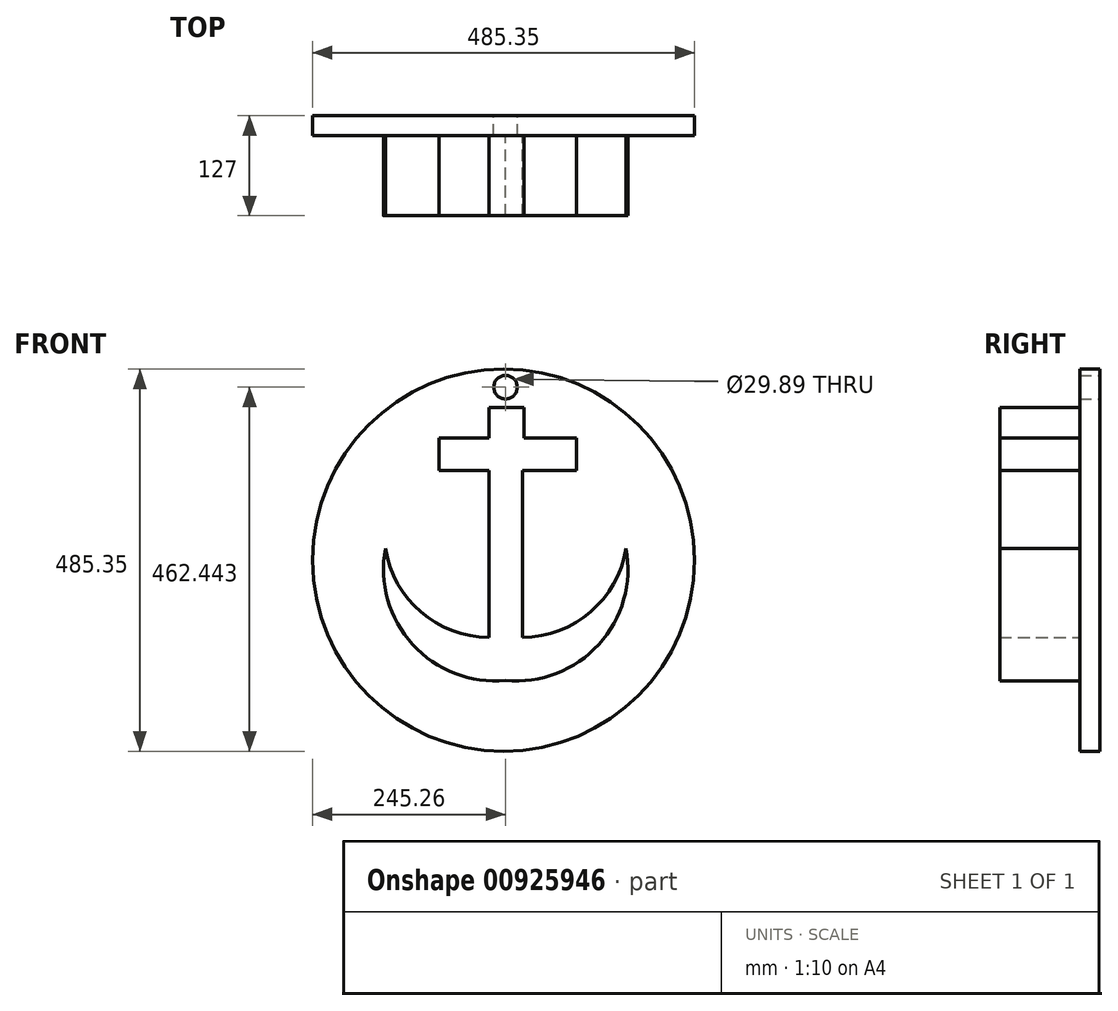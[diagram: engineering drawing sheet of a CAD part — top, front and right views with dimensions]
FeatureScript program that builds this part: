
annotation { "Feature Type Name" : "Feature", "Feature Type Description" : "" }
export const myFeature = defineFeature(function(context is Context, id is Id, definition is map)
    precondition{}
    {
        {
            var Q0;
            Q0=qCreatedBy(makeId("Front.planeOp"),FACE);
            var sketch = newSketch(context, id + "F0", { "sketchPlane" : qUnion([Q0])});
            skLineSegment(sketch, "E0", {"start": v(-148.32, 98.82) * mm, "end": v(-148.32, -113.03) * mm});
            skLineSegment(sketch, "E1.MirrorCS", {"start": v(-105.3, 98.82) * mm, "end": v(-105.3, -113.03) * mm});
            skArc(sketch, "E2", {"start": v(-279.63, 0) * mm, "mid": v(-234.63, -80.51) * mm, "end": v(-148.32, -113.03) * mm});
            skArc(sketch, "E3.MirrorCS", {"start": v(26, 0) * mm, "mid": v(-18.98, -80.51) * mm, "end": v(-105.3, -113.03) * mm});
            skArc(sketch, "E4", {"start": v(-279.63, 0) * mm, "mid": v(-245.04, -121.95) * mm, "end": v(-126.8, -167.65) * mm});
            skArc(sketch, "E5.MirrorCS", {"start": v(26, 0) * mm, "mid": v(-8.57, -121.95) * mm, "end": v(-126.8, -167.65) * mm});
            skLineSegment(sketch, "E6.bottom", {"start": v(-211.77, 140.2) * mm, "end": v(-148.32, 140.2) * mm});
            skLineSegment(sketch, "E6.top", {"start": v(-211.77, 98.82) * mm, "end": v(-148.32, 98.82) * mm});
            skLineSegment(sketch, "E6.left", {"start": v(-211.77, 140.2) * mm, "end": v(-211.77, 98.82) * mm});
            skLineSegment(sketch, "E6.right", {"start": v(-37.18, 140.2) * mm, "end": v(-37.18, 98.82) * mm});
            skLineSegment(sketch, "E7.trimOffspring", {"start": v(-105.3, 98.82) * mm, "end": v(-37.18, 98.82) * mm});
            skLineSegment(sketch, "E8.top", {"start": v(-148.32, 178.81) * mm, "end": v(-103.64, 178.81) * mm});
            skLineSegment(sketch, "E8.left", {"start": v(-148.32, 140.2) * mm, "end": v(-148.32, 178.81) * mm});
            skLineSegment(sketch, "E8.right", {"start": v(-103.64, 140.2) * mm, "end": v(-103.64, 178.81) * mm});
            skLineSegment(sketch, "E9.trimOffspring", {"start": v(-103.64, 140.2) * mm, "end": v(-37.18, 140.2) * mm});
            skSolve(sketch);
        }
        {
            var Q0;
            Q0 = qSketchRegion(id + "F0", true);
            extrude(context, id + "F1", {"entities" : qUnion([Q0]), "depth" : 127 * mm, "offsetDistance" : 25.4 * mm});
        }
        {
            var Q0;
            Q0=qCreatedBy(makeId("Front.planeOp"),FACE);
            var sketch = newSketch(context, id + "F2", { "sketchPlane" : qUnion([Q0])});
            skCircle(sketch, "E10", {"center": v(-129.65, -14.9) * mm, "radius": 242.68 * mm});
            skSolve(sketch);
        }
        {
            var Q0;
            Q0=makeQuery(id+"F2.imprint","IMPRINT",FACE,{"disambiguationData":[TD([[makeQuery(id+"F2.imprint","IMPRINT",EDGE,{"derivedFrom":sQuery(id+"F2.wireOp",EDGE,"E10")}),1.0]])]});
            extrude(context, id + "F3", {"entities" : qUnion([Q0]), "operationType" : NewBodyOperationType.ADD, "depth" : 25.4 * mm, "offsetDistance" : 25.4 * mm});
        }
        {
            var Q0;
            Q0=qCreatedBy(makeId("Front.planeOp"),FACE);
            var sketch = newSketch(context, id + "F4", { "sketchPlane" : qUnion([Q0])});
            skCircle(sketch, "E11", {"center": v(-127.06, 204.87) * mm, "radius": 14.94 * mm});
            skSolve(sketch);
        }
        {
            var Q0;
            Q0 = qSketchRegion(id + "F4", true);
            extrude(context, id + "F5", {"entities" : qUnion([Q0]), "operationType" : NewBodyOperationType.ADD, "depth" : 25.4 * mm, "offsetDistance" : 25.4 * mm});
        }
        {
            var Q0;
            Q0 = qSketchRegion(id + "F4", true);
            extrude(context, id + "F6", {"entities" : qUnion([Q0]), "operationType" : NewBodyOperationType.ADD, "depth" : 25.4 * mm, "offsetDistance" : 25.4 * mm});
        }
        {
            var Q0;
            Q0 = qSketchRegion(id + "F4", true);
            extrude(context, id + "F7", {"entities" : qUnion([Q0]), "operationType" : NewBodyOperationType.REMOVE, "endBound" : BoundingType.THROUGH_ALL, "depth" : 91.44 * mm, "offsetDistance" : 25.4 * mm});
        }
    });
